# Revit family: Silent Field 2.0
name_source: partatom
category: Apparecchi per illuminazione
revit_build: Autodesk Revit 2018 (Build: 20190510_1515(x64)
units: mm (PartAtom-declared; Revit-internal decimal feet)

## family parameters
Basato su piano di lavoro = Sì
Condiviso = No
Punto di calcolo locali = No
Quota connettore circolare = Usa diametro
Sempre verticale = Sì
Sorgente d'illuminazione = Sì
Taglio con vuoti quando caricato = No
Tipo di parte = Normale

## types (12) — shared parameters
6 Monthly = -
Air Handling = -
Angolo inclinazione = 90.00°
Annually = -
Application Environment = Internal
Beam Angle Longditudinal Axis  = 0.00°
Beam Angle Transverse Axis  = 0.00°
Bespoke Timeframe = -
CE Approval = YES
Colour Rendering Index = 90
Colour Temperature = 3000
Column = -
Control Gear Location = -
Control Gear Required = -
Control Gear Type = -
Daily = -
Daylight Sensor = -
Diffusing screen = -
ENEC Certification of European conformity = Y
Earth Point  = -
Emergency = N
Emergency Lighting Battery = -
End Caps/Transition Caps/Joints = -
Environmental Product Declaration = -
Expected Life = -
Face Shape = Circular
Features = -
Filtro dei colori = 16777215
Fire Rated = -
Fire Shroud = -
Fixings = -
Green Guide for Specification = -
Hazardous Area Category = -
Hazardous Area Protection Type = -
Housing Finish  = Welded fabric
Housing Material = Polyester fibre
IES Files  = https://www.artemide.com
IK Rating = -
IP Rating = IP20
IfcExportAs = IfcLightFixtureType
IfcExportType = NOT DEFINED
Infills = -
Integral Emergency Lighting Battery Type = -
Integral Fuse or Circuit Protection  = -
Intended Market = Unset
International Type Code = -
LED lifetime = 118000
Lamp Cap = LED Integrated
Lamp Included = Y
Lamp Replacement Interval = -
Lamp Survival Factor = -
Life Cycle Analysis = -
Light Fixture Mounting Type = Suspended
Light Output Pattern = -
Location of Manufacturer = -
Louvre/Lens = -
Luminaire Cleaning Interval  = -
Luminaire Type = Pendant
M_Diffuser = Artemide_Glass_LightBulb
M_Fixings = Artemide_Aluminum_Anodized
M_HousingStructure = Artemide_PolyesterFiberPET_Black
Maintenance Required: 0-300hrs  = -
Maintenance Required: 1001-2000hrs  = -
Maintenance Required: 2001-4000hrs  = -
Maintenance Required: 301-600hrs  = -
Maintenance Required: 4001-8000hrs  = -
Maintenance Required: 601-1000hrs = -
Maintenance Required: 8001-12000hrs  = -
Manufacturer Website = https://www.artemide.com
Material Ingredient Reporting = -
Max Height from ceiling = 2000 mm  [stored 6.56168 ft]
Monthly = -
Motion Detector = -
Motion Sensor = -
Number of Primary Lamps = 1
Overall Height = 500
Overall Length = 1000
Photocell = -
Power Supply Kit = -
Primary Lamp Type = LED
Product Literature = https://www.artemide.com
Produttore = Artemide
Prospetto di default = 1219 mm
Quarterly = -
Responsible Extraction of Materials = -
Responsible Sourcing of Materials = -
Secondary Lamp = N
Secondary Lamp Cap = -
Secondary Lamp Included = -
Secondary Lamp International Type Code = -
Service life  = -
Standards = -
Suitable Dimmer Type = Push
Suitable for Dimming  = Y
Suitable for Motion Detector Control = N
Suitable for Photocell Control = -
Testing method = -
URL to Energy Technology List = -
URL to O&M Manual = https://www.artemide.com
Uniclass 2015 = Pr_70_70_48
Unified Glare Rating  = -
Variazione temperatura colore lampada con luminosità attenuata = <Nessuno>
Voltage = -
Warranty ID = https://cloud.artemide.com
Weekly = -
zero-valued in all types: Access Clearance Bottom, Access Clearance Front, Access Clearance Left, Access Clearance Rear, Access Clearance Right, Access Clearance Top, Ambient Temperature                            , Basis of lifetime lumen depreciation  , Basis of lifetime luminaire failures       , Control Gear Standby Power , Current , Cut Out Length, Cut Out Width, Downward Component, Drive Current                                         , Duration of Integral Emergency Lighting , Embodied Carbon , Emergency Charging Power      , Emergency light output percentage, External Control Line Voltage, Face Length, Face Width, Fire Rated Temperature, Fire Rating Duration, Frequency , Input Lumens Indirect light, LED Initial Colour Variation                     , LED Maintained Colour Variation        , Luminaire Maintenance Factor, Luminance at 65deg Angle, Maximum Operating Temperature, Minimum Operating Temperature, Number of Poles, Number of Secondary Lamps, Output Lumens Indirect light, Overall Light Output Ratio, Overall Width, Power Factor, Secondary Lamp Colour Rendering Index, Secondary Lamp Colour Temperature, Secondary Lamp Efficacy, Secondary Lamp Initial Lumens , Secondary Lamp Voltage, Secondary Rated Lamp Life, Shipping Weight, Supply Phase, Total Light Output , Total Power, Upward Component 

## per-type parameters (varying)
| type | Efficiency | File diagramma fotometrico | Gross Weight | Housing Colour  | Initial Lumens | Input Lumens Direct light | M_Housing | Output Lumens Direct light | Product Model Number | Product Range | Rated Lamp Life |
| SilentField2.0_Direct_3000K_White_1014020A | 64 | 1014020A.IES | 7.8 | White | 2085 | 3270 | Artemide_PolyesterFiberPET_White | 2085 | 1014020A | SilentField2.3 | 118000 |
| SilentField2.0_Direct_3000K_Orange_1014040A | 64 | 1014040A.IES | 7.8 | Orange | 2085 | 3270 | Artemide_PolyesterFiberPET_Orange | 2085 | 1014040A | SilentField2.4 | 118000 |
| SilentField2.0_Direct_3000K_Black_1014030A | 64 | 1014030A.IES | 7.8 | Black | 2085 | 3270 | Artemide_PolyesterFiberPET_Black | 2085 | 1014030A | SilentField2.5 | 118000 |
| SilentField2.0_Direct+Indirect_3000K_White_1013020A | 75 | 1013020A.IES | 8.46 | White | 5276 | 7016.8 | Artemide_PolyesterFiberPET_White | 5276 | 1013020A | SilentField2.0 | 50000 |
| SilentField2.0_Direct+Indirect_3000K_Orange_1013040A | 75 | 1013040A.IES | 8.46 | Orange | 5276 | 7016.8 | Artemide_PolyesterFiberPET_Orange | 5276 | 1013040A | SilentField2.1 | 50000 |
| SilentField2.0_Direct+Indirect_3000K_Black_1013030A | 75 | 1013030A.IES | 8.46 | Black | 5276 | 7016.8 | Artemide_PolyesterFiberPET_Black | 5276 | 1013030A | SilentField2.2 | 50000 |
| SilentField2.0_Direct_3000K_APPCompatible_White_1014020APP | 64 | 1014020APP.IES | 7.8 | White | 2085 | 3270 | Artemide_PolyesterFiberPET_White | 2085 | 1014020APP | SilentField2.7 | 118000 |
| SilentField2.0_Direct_3000K_APPCompatible_Orange_1014040APP | 64 | 1014040APP.IES | 7.8 | Orange | 2085 | 3270 | Artemide_PolyesterFiberPET_Orange | 2085 | 1014040APP | SilentField2.9 | 118000 |
| SilentField2.0_Direct_3000K_APPCompatible_Black_1014030APP | 64 | 1014030APP.IES | 7.8 | Black | 2085 | 3270 | Artemide_PolyesterFiberPET_Black | 2085 | 1014030APP | SilentField2.11 | 118000 |
| SilentField2.0_Direct+Indirect_3000K_APPCompatible_White_1013020APP | 75 | 1013020APP.IES | 8.46 | White | 5276 | 7016.8 | Artemide_PolyesterFiberPET_White | 5276 | 1013020APP | SilentField2.6 | 50000 |
| SilentField2.0_Direct+Indirect_3000K_APPCompatible_Orange_1013040APP | 75 | 1013040APP.IES | 8.46 | Orange | 5276 | 7016.8 | Artemide_PolyesterFiberPET_Orange | 5276 | 1013040APP | SilentField2.8 | 50000 |
| SilentField2.0_Direct+Indirect_3000K_APPCompatible_Black_1013030APP | 75 | 1013030APP.IES | 8.46 | Black | 5276 | 7016.8 | Artemide_PolyesterFiberPET_Black | 5276 | 1013030APP | SilentField2.10 | 50000 |

note: [stored X ft] marks values corroborated as IEEE doubles in the binary element streams (Revit-internal decimal feet)

## geometry (parser evidence)
native form markers: Sweep x3
no freeform markers — native parametric forms only
